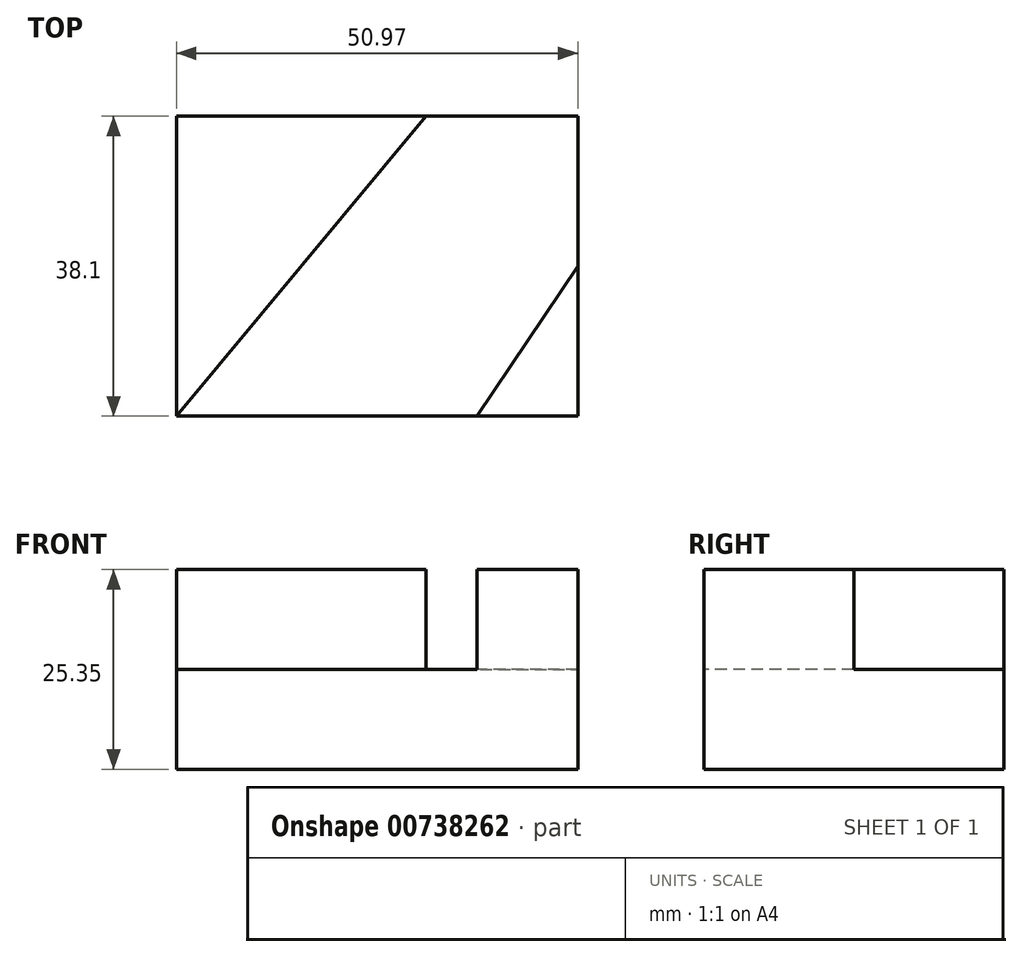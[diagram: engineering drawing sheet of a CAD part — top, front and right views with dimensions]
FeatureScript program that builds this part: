
annotation { "Feature Type Name" : "Feature", "Feature Type Description" : "" }
export const myFeature = defineFeature(function(context is Context, id is Id, definition is map)
    precondition{}
    {
        {
            var Q0;
            Q0=qCreatedBy(makeId("Front.planeOp"),FACE);
            var sketch = newSketch(context, id + "F0", { "sketchPlane" : qUnion([Q0])});
            skLineSegment(sketch, "E0", {"start": v(0, 0) * mm, "end": v(-50.97, 0) * mm});
            skLineSegment(sketch, "E1", {"start": v(-50.97, 0) * mm, "end": v(-50.97, 25.35) * mm});
            skLineSegment(sketch, "E2", {"start": v(-50.97, 25.35) * mm, "end": v(0, 25.35) * mm});
            skLineSegment(sketch, "E3", {"start": v(0, 25.35) * mm, "end": v(0, 0) * mm});
            skSolve(sketch);
        }
        {
            var Q0;
            Q0 = qSketchRegion(id + "F0", true);
            extrude(context, id + "F1", {"entities" : qUnion([Q0]), "oppositeDirection" : true, "depth" : 38.1 * mm, "offsetDistance" : 25.4 * mm});
        }
        {
            var Q0;
            Q0=makeQuery(id+"F1.opExtrude","SWEPT_FACE",FACE,{"disambiguationData":[OSD([sQuery(id+"F0.wireOp",EDGE,"E2")])]});
            var sketch = newSketch(context, id + "F2", { "sketchPlane" : qUnion([Q0])});
            skLineSegment(sketch, "E4", {"start": v(0, 0) * mm, "end": v(-12.81, 0) * mm});
            skLineSegment(sketch, "E5", {"start": v(0, 0) * mm, "end": v(0, 19.05) * mm});
            skLineSegment(sketch, "E6", {"start": v(0, 19.05) * mm, "end": v(-12.81, 0) * mm});
            skLineSegment(sketch, "E7", {"start": v(-50.97, 38.1) * mm, "end": v(-19.27, 38.1) * mm});
            skLineSegment(sketch, "E8", {"start": v(-50.97, 0) * mm, "end": v(-50.97, 38.1) * mm});
            skLineSegment(sketch, "E9", {"start": v(-50.97, 0) * mm, "end": v(-19.27, 38.1) * mm});
            skSolve(sketch);
        }
        {
            var Q0;
            {var subQ4=sQuery(id+"F2.wireOp",EDGE,"E6");Q0=makeQuery(id+"F2.imprint","IMPRINT",FACE,{"disambiguationData":[TD([[makeQuery(id+"F2.imprint","IMPRINT",EDGE,{"derivedFrom":subQ4}),-1.0]])]});}
            extrude(context, id + "F3", {"entities" : qUnion([Q0]), "operationType" : NewBodyOperationType.REMOVE, "oppositeDirection" : true, "depth" : 12.7 * mm, "offsetDistance" : 25.4 * mm});
        }
    });
